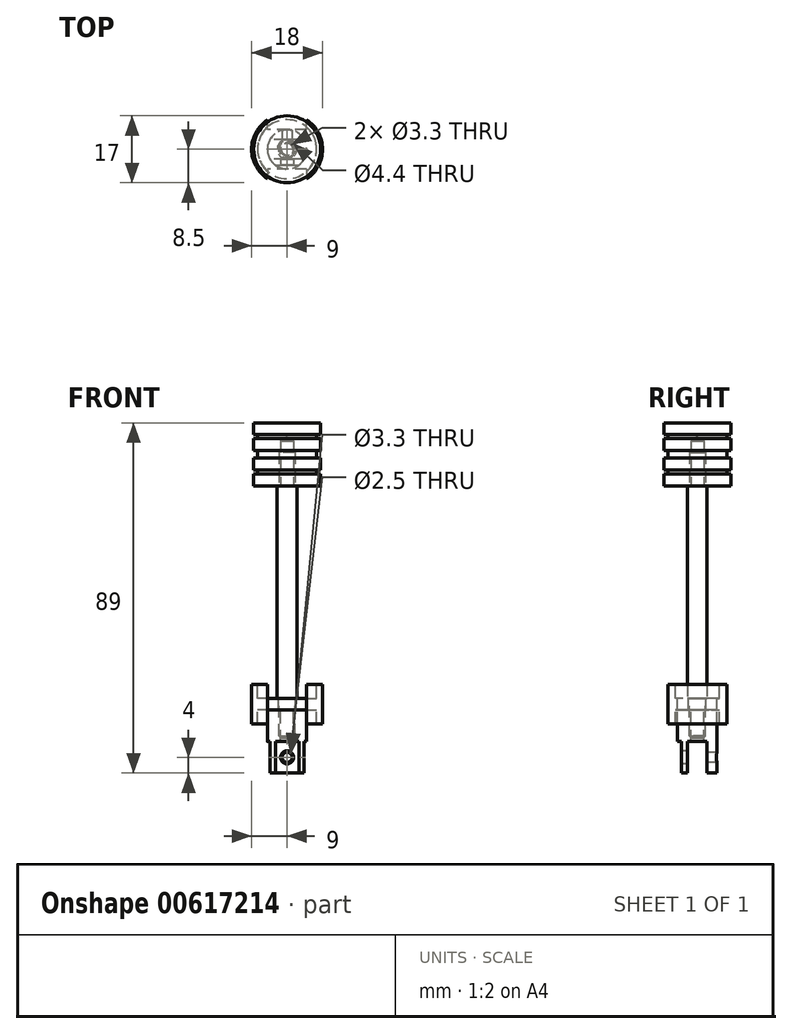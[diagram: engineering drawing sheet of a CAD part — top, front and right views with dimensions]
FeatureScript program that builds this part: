
annotation { "Feature Type Name" : "Feature", "Feature Type Description" : "" }
export const myFeature = defineFeature(function(context is Context, id is Id, definition is map)
    precondition{}
    {
        {
            var Q0;
            Q0=qCreatedBy(makeId("Front.planeOp"),FACE);
            var sketch = newSketch(context, id + "F0", { "sketchPlane" : qUnion([Q0])});
            skLineSegment(sketch, "E0", {"start": v(0, 11.26) * mm, "end": v(0, -14.67) * mm, "construction": true});
            skLineSegment(sketch, "E1", {"start": v(0, 1.5) * mm, "end": v(0, -1.5) * mm});
            skLineSegment(sketch, "E2", {"start": v(0, -1.5) * mm, "end": v(7.5, -1.5) * mm});
            skLineSegment(sketch, "E3", {"start": v(7.5, -1.5) * mm, "end": v(7.5, -5) * mm});
            skLineSegment(sketch, "E4", {"start": v(7.5, -5) * mm, "end": v(9, -5) * mm});
            skLineSegment(sketch, "E5", {"start": v(0, 0) * mm, "end": v(16.92, 0) * mm, "construction": true});
            skLineSegment(sketch, "E6.MirrorCS", {"start": v(0, 1.5) * mm, "end": v(7.5, 1.5) * mm});
            skLineSegment(sketch, "E7.MirrorCS", {"start": v(7.5, 1.5) * mm, "end": v(7.5, 5) * mm});
            skLineSegment(sketch, "E8.MirrorCS", {"start": v(7.5, 5) * mm, "end": v(9, 5) * mm});
            skLineSegment(sketch, "E9", {"start": v(9, 5) * mm, "end": v(9, -5) * mm});
            skSolve(sketch);
        }
        {
            var Q0;
            Q0 = qSketchRegion(id + "F0", true);
            var Q1;
            Q1=sQuery(id+"F0.wireOp",EDGE,"E0");
            revolve(context, id + "F1", {"entities" : qUnion([Q0]), "axis" : qUnion([Q1]), "revolveType" : RevolveType.FULL});
        }
        {
            var Q0;
            Q0=makeQuery(id+"F1.opRevolve","SWEPT_FACE",FACE,{"disambiguationData":[OSD([sQuery(id+"F0.wireOp",EDGE,"E6.MirrorCS")])]});
            var sketch = newSketch(context, id + "F2", { "sketchPlane" : qUnion([Q0])});
            skPoint(sketch, "E10", {"position": v(0, 0) * mm});
            skSolve(sketch);
        }
        {
            var Q0;
            Q0=sQuery(id+"F2.wireOp",VERTEX,"E10");
            var Q1;
            Q1=makeQuery(id+"F1.opRevolve","SWEPT_BODY",BODY,{"disambiguationData":[OSD([sQuery(id+"F0.wireOp",EDGE,"E1"),sQuery(id+"F0.wireOp",EDGE,"E2"),sQuery(id+"F0.wireOp",EDGE,"E3"),sQuery(id+"F0.wireOp",EDGE,"E4"),sQuery(id+"F0.wireOp",EDGE,"E6.MirrorCS"),sQuery(id+"F0.wireOp",EDGE,"E7.MirrorCS"),sQuery(id+"F0.wireOp",EDGE,"E8.MirrorCS"),sQuery(id+"F0.wireOp",EDGE,"E9")])]});
            hole(context, id + "F3", {"style" : HoleStyle.SIMPLE, "endStyle" : HoleEndStyle.THROUGH, "standardTappedOrClearance" : lookupTablePath({ "standard" : "ISO", "fit" : "Normal", "size" : "M4", "type" : "Clearance" }), "standardBlindInLast" : lookupTablePath({ "fit" : "Standard", "standard" : "ISO", "size" : "M4", "type" : "Clearance" }), "holeDiameter" : 4.4 * mm, "majorDiameter" : 4 * mm, "isTappedThrough" : true, "tappedDepth" : 7 * mm, "tapClearance" : 2, "locations" : qUnion([Q0]), "scope" : qUnion([Q1])});
        }
        {
            var Q0;
            Q0=makeQuery(id+"F1.opRevolve","SWEPT_FACE",FACE,{"disambiguationData":[OSD([sQuery(id+"F0.wireOp",EDGE,"E8.MirrorCS")])]});
            var sketch = newSketch(context, id + "F4", { "sketchPlane" : qUnion([Q0])});
            skLineSegment(sketch, "E11.bottom", {"start": v(5, 5) * mm, "end": v(-5, 5) * mm});
            skLineSegment(sketch, "E11.top", {"start": v(5, 15) * mm, "end": v(-5, 15) * mm});
            skLineSegment(sketch, "E11.left", {"start": v(5, 5) * mm, "end": v(5, 15) * mm});
            skLineSegment(sketch, "E11.right", {"start": v(-5, 5) * mm, "end": v(-5, 15) * mm});
            skLineSegment(sketch, "E12", {"start": v(-10.45, 0) * mm, "end": v(10.9, 0) * mm, "construction": true});
            skLineSegment(sketch, "E13", {"start": v(0, 0) * mm, "end": v(0, 15) * mm, "construction": true});
            skLineSegment(sketch, "E14.MirrorCS", {"start": v(5, -5) * mm, "end": v(-5, -5) * mm});
            skLineSegment(sketch, "E15.MirrorCS", {"start": v(5, -5) * mm, "end": v(5, -15) * mm});
            skLineSegment(sketch, "E16.MirrorCS", {"start": v(5, -15) * mm, "end": v(-5, -15) * mm});
            skLineSegment(sketch, "E17.MirrorCS", {"start": v(-5, -5) * mm, "end": v(-5, -15) * mm});
            skSolve(sketch);
        }
        {
            var Q0;
            Q0 = qSketchRegion(id + "F4", true);
            extrude(context, id + "F5", {"entities" : qUnion([Q0]), "operationType" : NewBodyOperationType.REMOVE, "endBound" : BoundingType.THROUGH_ALL, "oppositeDirection" : true, "depth" : 25 * mm, "offsetDistance" : 25 * mm});
        }
        {
            var Q0;
            Q0=makeQuery(id+"F1.opRevolve","SWEPT_FACE",FACE,{"disambiguationData":[OSD([sQuery(id+"F0.wireOp",EDGE,"E6.MirrorCS")])]});
            var sketch = newSketch(context, id + "F6", { "sketchPlane" : qUnion([Q0])});
            skCircle(sketch, "E18", {"center": v(0, 0) * mm, "radius": 2.5 * mm});
            skSolve(sketch);
        }
        {
            var Q0;
            Q0 = qSketchRegion(id + "F6", true);
            extrude(context, id + "F7", {"entities" : qUnion([Q0]), "depth" : 54 * mm, "offsetDistance" : 25 * mm});
        }
        {
            var Q0;
            Q0=makeQuery(id+"F7.opExtrude","CAP_FACE",FACE,{"disambiguationData":[OSD([sQuery(id+"F6.wireOp",EDGE,"E18")])],"isStart":true});
            var sketch = newSketch(context, id + "F8", { "sketchPlane" : qUnion([Q0])});
            skCircle(sketch, "E19", {"center": v(0, 0) * mm, "radius": 2 * mm});
            skSolve(sketch);
        }
        {
            var Q0;
            Q0 = qSketchRegion(id + "F8", true);
            extrude(context, id + "F9", {"entities" : qUnion([Q0]), "operationType" : NewBodyOperationType.ADD, "depth" : 10 * mm, "offsetDistance" : 25 * mm});
        }
        {
            var Q0;
            Q0=makeQuery(id+"F7.opExtrude","CAP_FACE",FACE,{"disambiguationData":[OSD([sQuery(id+"F6.wireOp",EDGE,"E18")])],"isStart":false});
            var sketch = newSketch(context, id + "F10", { "sketchPlane" : qUnion([Q0])});
            skCircle(sketch, "E20", {"center": v(0, 0) * mm, "radius": 2 * mm});
            skSolve(sketch);
        }
        {
            var Q0;
            Q0 = qSketchRegion(id + "F10", true);
            extrude(context, id + "F11", {"entities" : qUnion([Q0]), "operationType" : NewBodyOperationType.ADD, "depth" : 9 * mm, "offsetDistance" : 25 * mm});
        }
        {
            var Q0;
            Q0=makeQuery(id+"F9.opExtrude","CAP_EDGE",EDGE,{"disambiguationData":[OSD([sQuery(id+"F8.wireOp",EDGE,"E19")])],"isStart":false});
            var Q1;
            Q1=makeQuery(id+"F11.opExtrude","CAP_EDGE",EDGE,{"disambiguationData":[OSD([sQuery(id+"F10.wireOp",EDGE,"E20")])],"isStart":false});
            chamfer(context, id + "F12", {"entities" : qUnion([Q0, Q1]), "width" : .5 * mm, "tangentPropagation" : true});
        }
        {
            var Q0;
            Q0=makeQuery(id+"F7.opExtrude","CAP_FACE",FACE,{"disambiguationData":[OSD([sQuery(id+"F6.wireOp",EDGE,"E18")])],"isStart":false});
            var sketch = newSketch(context, id + "F13", { "sketchPlane" : qUnion([Q0])});
            skCircle(sketch, "E21", {"center": v(0, 0) * mm, "radius": 8.5 * mm});
            skSolve(sketch);
        }
        {
            var Q0;
            Q0 = qSketchRegion(id + "F13", true);
            extrude(context, id + "F14", {"entities" : qUnion([Q0]), "depth" : 16 * mm, "offsetDistance" : 25 * mm});
        }
        {
            var Q0;
            Q0=qCreatedBy(makeId("Front.planeOp"),FACE);
            var sketch = newSketch(context, id + "F15", { "sketchPlane" : qUnion([Q0])});
            skLineSegment(sketch, "E22.bottom", {"start": v(11.5, 58.5) * mm, "end": v(7.5, 58.5) * mm});
            skLineSegment(sketch, "E22.top", {"start": v(11.5, 59.5) * mm, "end": v(7.5, 59.5) * mm});
            skLineSegment(sketch, "E22.left", {"start": v(11.5, 58.5) * mm, "end": v(11.5, 59.5) * mm});
            skLineSegment(sketch, "E22.right", {"start": v(7.5, 58.5) * mm, "end": v(7.5, 59.5) * mm});
            skPoint(sketch, "E22.middle", {"position": v(9.5, 59) * mm});
            skLineSegment(sketch, "E23", {"start": v(0, 71.5) * mm, "end": v(0, 55.5) * mm, "construction": true});
            skLineSegment(sketch, "E24", {"start": v(0, 63.5) * mm, "end": v(11.5, 63.5) * mm, "construction": true});
            skPoint(sketch, "E24.endSnap0", {"position": v(0, 63.5) * mm});
            skPoint(sketch, "E25.MirrorP", {"position": v(9.5, 68) * mm});
            skLineSegment(sketch, "E26.MirrorCS", {"start": v(11.5, 68.5) * mm, "end": v(7.5, 68.5) * mm});
            skLineSegment(sketch, "E27.MirrorCS", {"start": v(11.5, 67.5) * mm, "end": v(7.5, 67.5) * mm});
            skLineSegment(sketch, "E28.MirrorCS", {"start": v(11.5, 68.5) * mm, "end": v(11.5, 67.5) * mm});
            skLineSegment(sketch, "E29.MirrorCS", {"start": v(7.5, 68.5) * mm, "end": v(7.5, 67.5) * mm});
            skLineSegment(sketch, "E30.bottom", {"start": v(11.5, 62.5) * mm, "end": v(7.5, 62.5) * mm});
            skLineSegment(sketch, "E30.top", {"start": v(11.5, 64.5) * mm, "end": v(7.5, 64.5) * mm});
            skLineSegment(sketch, "E30.left", {"start": v(11.5, 62.5) * mm, "end": v(11.5, 64.5) * mm});
            skLineSegment(sketch, "E30.right", {"start": v(7.5, 62.5) * mm, "end": v(7.5, 64.5) * mm});
            skPoint(sketch, "E30.middle", {"position": v(9.5, 63.5) * mm});
            skPoint(sketch, "E30.middle.positionSnap0", {"position": v(9.5, 59.5) * mm});
            skPoint(sketch, "E30.centerSnap0", {"position": v(9.5, 59.5) * mm});
            skSolve(sketch);
        }
        {
            var Q0;
            Q0 = qSketchRegion(id + "F15", true);
            var Q1;
            Q1=sQuery(id+"F15.wireOp",EDGE,"E23");
            revolve(context, id + "F16", {"operationType" : NewBodyOperationType.REMOVE, "entities" : qUnion([Q0]), "axis" : qUnion([Q1]), "revolveType" : RevolveType.FULL, "oppositeDirection" : true});
        }
        {
            var Q0;
            Q0=sQuery(id+"F10.wireOp",VERTEX,"E20.center");
            var Q1;
            Q1=makeQuery(id+"F14.opExtrude","SWEPT_BODY",BODY,{"disambiguationData":[OSD([sQuery(id+"F13.wireOp",EDGE,"E21")])]});
            hole(context, id + "F17", {"style" : HoleStyle.SIMPLE, "endStyle" : HoleEndStyle.BLIND, "oppositeDirection" : true, "standardTappedOrClearance" : lookupTablePath({ "standard" : "ISO", "engagement" : "75%", "pitch" : "0.7 mm", "size" : "M4", "type" : "Tapped" }), "standardBlindInLast" : lookupTablePath({ "standard" : "ISO", "engagement" : "75%", "pitch" : "0.7 mm", "size" : "M4", "type" : "Tapped" }), "holeDiameter" : 3.3 * mm, "majorDiameter" : 4 * mm, "showTappedDepth" : true, "holeDepth" : 11.4 * mm, "isTappedThrough" : true, "tappedDepth" : 10 * mm, "tapClearance" : 2, "locations" : qUnion([Q0]), "scope" : qUnion([Q1])});
        }
        {
            var Q0;
            Q0=makeQuery(id+"F1.opRevolve","SWEPT_FACE",FACE,{"disambiguationData":[OSD([sQuery(id+"F0.wireOp",EDGE,"E2")])]});
            var sketch = newSketch(context, id + "F18", { "sketchPlane" : qUnion([Q0])});
            skCircle(sketch, "E31", {"center": v(0, 0) * mm, "radius": 5 * mm});
            skSolve(sketch);
        }
        {
            var Q0;
            Q0 = qSketchRegion(id + "F18", true);
            extrude(context, id + "F19", {"entities" : qUnion([Q0]), "depth" : 16 * mm, "offsetDistance" : 25 * mm});
        }
        {
            var Q0;
            Q0=qCreatedBy(makeId("Right.planeOp"),FACE);
            var sketch = newSketch(context, id + "F20", { "sketchPlane" : qUnion([Q0])});
            skLineSegment(sketch, "E32.bottom", {"start": v(2.5, -17.5) * mm, "end": v(-2.5, -17.5) * mm});
            skLineSegment(sketch, "E32.top", {"start": v(2.5, -9.5) * mm, "end": v(-2.5, -9.5) * mm});
            skLineSegment(sketch, "E32.left", {"start": v(2.5, -17.5) * mm, "end": v(2.5, -9.5) * mm});
            skLineSegment(sketch, "E32.right", {"start": v(-2.5, -17.5) * mm, "end": v(-2.5, -9.5) * mm});
            skPoint(sketch, "E32.middle", {"position": v(0, -13.5) * mm});
            skSolve(sketch);
        }
        {
            var Q0;
            Q0 = qSketchRegion(id + "F20", true);
            extrude(context, id + "F21", {"entities" : qUnion([Q0]), "operationType" : NewBodyOperationType.REMOVE, "endBound" : BoundingType.THROUGH_ALL, "depth" : 25 * mm, "offsetDistance" : 25 * mm, "hasSecondDirection" : true, "secondDirectionBound" : SecondDirectionBoundingType.THROUGH_ALL, "secondDirectionOppositeDirection" : true, "secondDirectionDepth" : 25 * mm});
        }
        {
            var Q0;
            {var subQ0=sQuery(id+"F18.wireOp",EDGE,"E31");Q0=makeQuery(id+"F21.boolean.opBoolean","SPLIT",FACE,{"disambiguationData":[TD([makeQuery(id+"F21.opExtrude","SWEPT_FACE",FACE,{"disambiguationData":[OSD([sQuery(id+"F20.wireOp",EDGE,"E32.right")])]})])],"derivedFrom":makeQuery(id+"F19.opExtrude","CAP_FACE",FACE,{"disambiguationData":[OSD([subQ0])],"isStart":false})});}
            var sketch = newSketch(context, id + "F22", { "sketchPlane" : qUnion([Q0])});
            skArc(sketch, "E33.0", {"start": v(3, 4) * mm, "mid": v(0, 5) * mm, "end": v(-3, 4) * mm});
            skLineSegment(sketch, "E34", {"start": v(-3, 4) * mm, "end": v(3, 4) * mm});
            skPoint(sketch, "E35.orphan", {"position": v(4.33, 2.5) * mm});
            skPoint(sketch, "E36.orphan", {"position": v(-4.33, 2.5) * mm});
            skSolve(sketch);
        }
        {
            var Q0;
            Q0 = qSketchRegion(id + "F22", true);
            var Q1;
            Q1=makeQuery(id+"F21.boolean.opBoolean","INTERSECT",VERTEX,{"disambiguationData":[OD(1.0)],"derivedFrom":[makeQuery(id+"F19.opExtrude","SWEPT_FACE",FACE,{"disambiguationData":[OSD([sQuery(id+"F18.wireOp",EDGE,"E31")])]}),makeQuery(id+"F21.opExtrude","SWEPT_FACE",FACE,{"disambiguationData":[OSD([sQuery(id+"F20.wireOp",EDGE,"E32.top")])]}),makeQuery(id+"F21.opExtrude","SWEPT_FACE",FACE,{"disambiguationData":[OSD([sQuery(id+"F20.wireOp",EDGE,"E32.right")])]})]});
            extrude(context, id + "F23", {"entities" : qUnion([Q0]), "operationType" : NewBodyOperationType.REMOVE, "endBound" : BoundingType.UP_TO_VERTEX, "oppositeDirection" : true, "depth" : 25 * mm, "endBoundEntityVertex" : qUnion([Q1]), "offsetDistance" : 25 * mm});
        }
        {
            var Q0;
            Q0=makeQuery(id+"F23.boolean.opBoolean","COPY",FACE,{"derivedFrom":makeQuery(id+"F23.opExtrude","SWEPT_FACE",FACE,{"disambiguationData":[OSD([sQuery(id+"F22.wireOp",EDGE,"E34")])]})});
            var sketch = newSketch(context, id + "F24", { "sketchPlane" : qUnion([Q0])});
            skLineSegment(sketch, "E37", {"start": v(0, -9.5) * mm, "end": v(0, -17.5) * mm, "construction": true});
            skPoint(sketch, "E38", {"position": v(0, -13.5) * mm});
            skSolve(sketch);
        }
        {
            var Q0;
            Q0=sQuery(id+"F24.wireOp",VERTEX,"E38");
            var Q1;
            Q1=makeQuery(id+"F19.opExtrude","SWEPT_BODY",BODY,{"disambiguationData":[OSD([sQuery(id+"F18.wireOp",EDGE,"E31")])]});
            hole(context, id + "F25", {"style" : HoleStyle.SIMPLE, "endStyle" : HoleEndStyle.BLIND, "standardTappedOrClearance" : lookupTablePath({ "standard" : "ISO", "fit" : "Normal", "size" : "M3", "type" : "Clearance" }), "standardBlindInLast" : lookupTablePath({ "fit" : "Standard", "standard" : "ISO", "size" : "M3", "type" : "Clearance" }), "holeDiameter" : 3.3 * mm, "majorDiameter" : 5 * mm, "holeDepth" : 5 * mm, "isTappedThrough" : true, "tappedDepth" : 7 * mm, "tapClearance" : 2, "locations" : qUnion([Q0]), "scope" : qUnion([Q1])});
        }
        {
            var Q0;
            Q0=sQuery(id+"F24.wireOp",VERTEX,"E38");
            var Q1;
            Q1=makeQuery(id+"F19.opExtrude","SWEPT_BODY",BODY,{"disambiguationData":[OSD([sQuery(id+"F18.wireOp",EDGE,"E31")])]});
            hole(context, id + "F26", {"style" : HoleStyle.SIMPLE, "endStyle" : HoleEndStyle.THROUGH, "standardTappedOrClearance" : lookupTablePath({ "standard" : "ISO", "engagement" : "75%", "pitch" : "0.5 mm", "size" : "M3", "type" : "Tapped" }), "standardBlindInLast" : lookupTablePath({ "standard" : "ISO", "engagement" : "75%", "pitch" : "0.5 mm", "size" : "M3", "type" : "Tapped" }), "holeDiameter" : 2.5 * mm, "majorDiameter" : 3 * mm, "showTappedDepth" : true, "isTappedThrough" : true, "tappedDepth" : 7 * mm, "tapClearance" : 2, "locations" : qUnion([Q0]), "scope" : qUnion([Q1])});
        }
        {
            var Q0;
            Q0=sQuery(id+"F10.wireOp",VERTEX,"E20.center");
            var Q1;
            Q1=makeQuery(id+"F19.opExtrude","SWEPT_BODY",BODY,{"disambiguationData":[OSD([sQuery(id+"F18.wireOp",EDGE,"E31")])]});
            hole(context, id + "F27", {"style" : HoleStyle.SIMPLE, "endStyle" : HoleEndStyle.THROUGH, "standardTappedOrClearance" : lookupTablePath({ "standard" : "ISO", "engagement" : "75%", "pitch" : "0.7 mm", "size" : "M4", "type" : "Tapped" }), "standardBlindInLast" : lookupTablePath({ "standard" : "ISO", "engagement" : "75%", "pitch" : "0.7 mm", "size" : "M4", "type" : "Tapped" }), "holeDiameter" : 3.3 * mm, "majorDiameter" : 4 * mm, "showTappedDepth" : true, "isTappedThrough" : true, "tappedDepth" : 7 * mm, "tapClearance" : 2, "locations" : qUnion([Q0]), "scope" : qUnion([Q1])});
        }
    });
